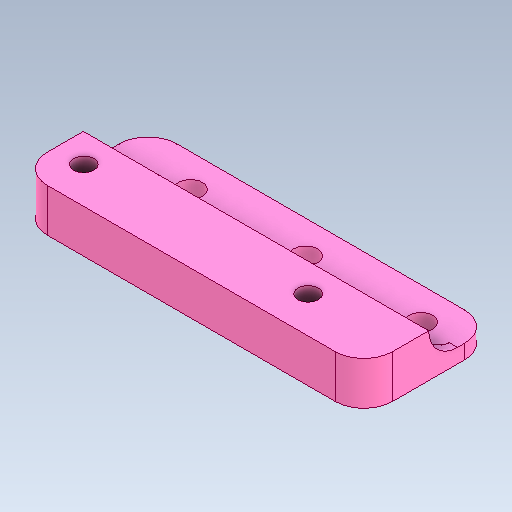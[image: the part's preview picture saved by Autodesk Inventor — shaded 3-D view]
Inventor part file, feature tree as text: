
AUTODESK INVENTOR PART (.ipt)
format: ipt  version: 2023 (Build 270158000, 158)  size: 147,456 bytes
history: native  units: in
note: dims shown in document units (in); Inventor stores cm internally (conversion verified against a paired STEP export)
features: other x3, sketch x3
ambient origin geometry x8: Origin, YZ Plane, XZ Plane, XY Plane, X Axis, Y Axis, Z Axis, Center Point
bodies: Solid1 (feature_tree)
feature tree (6):
  other  "DriveMotorMount5_MIR1.ipt"
  other  "Solid1::DriveMotorMount5_MIR1.ipt"
  other  "TaggingFeature1"
  sketch  "Sketch1"  dims[d0=0.3937in]
  sketch  "Sketch2"
  sketch  "Sketch3"
